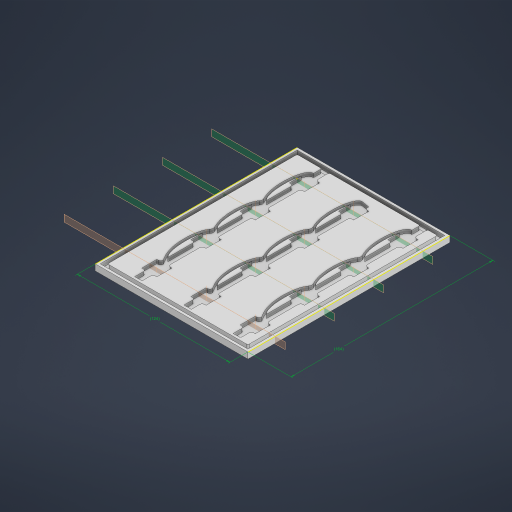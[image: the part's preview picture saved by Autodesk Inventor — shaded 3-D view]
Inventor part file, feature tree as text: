
AUTODESK INVENTOR PART (.ipt)
format: ipt  version: 2023 (Build 270158030, 158C)  size: 1,356,800 bytes
history: native  units: mm
features: other x13, sketch x8, plane x7, extrude x6, delete_face x5, fillet x3, direct_edit x3, pattern_linear x2, projected_geometry x2, move_body x2, chamfer x1
ambient origin geometry x8: Origin, YZ Plane, XZ Plane, XY Plane, X Axis, Y Axis, Z Axis, Center Point
bodies: Volumenkörper1 (feature_tree)
feature tree (52):
  extrude  "Extrusion1"  Depth=12.3mm
  extrude  "Extrusion2"  Depth=120.0mm
  extrude  "Extrusion3"  Depth=3.0mm TaperAngle=0.0deg
  chamfer  "Fase1"  Distance=2.0mm
  fillet  "Rundung1"  Radius=6.0mm
  pattern_linear  "Rechteckige Anordnung2"  Count1=3  [1 undecoded]
  extrude  "Extrusion5"  Depth=1.25mm
  direct_edit  "Direktbearbeitung1"
  sketch  "Sketch12"  dims[d18=10.0mm d19=0.0mm]
  extrude  "Extrusion11"  Depth=1.25mm
  delete_face  "Delete Face1"
  pattern_linear  "Rectangular Pattern4"  Spacing1=3.5mm  [1 undecoded]
  delete_face  "Delete Face2"
  fillet  "Fillet3"  Radius=8.5mm
  delete_face  "Delete Face3"
  delete_face  "Delete Face4"
  extrude  "Extrusion16"  Depth=1.25mm TaperAngle=0.0deg
  direct_edit  "Direct Edit3"
  delete_face  "Delete Face5"
  direct_edit  "Direct Edit4"
  fillet  "Fillet7"  Radius=30.0mm
  plane  "Work Plane1"
  plane  "Work Plane2"
  plane  "Work Plane3"
  plane  "Work Plane4"
  plane  "Work Plane5"
  plane  "Work Plane6"
  other  "Work Axis1"
  other  "Work Axis2"
  other  "Work Axis3"
  other  "Work Axis4"
  other  "Work Axis5"
  other  "Work Axis6"
  other  "Work Axis7"
  other  "Work Axis8"
  plane  "Work Plane7"
  other  "Work Axis9"
  other  "Work Axis10"
  other  "Work Axis11"
  sketch  "Sketch19"  dims[d33=40.0mm d35=40.0mm d49=3.0mm d50=2.0mm d51=3.5mm d52=0.0mm d53=8.5mm d54=0.0mm d55=0.0mm d124=3.5mm d125=0.0mm d126=30.0mm d128=40.0mm d129=30.0mm d131=40.0mm d139=3.0mm d162=2.0mm d163=10.0mm d164=0.0mm d165=-1.0mm d175=-2.5mm d176=0.0mm d177=0.0mm d181=1.25mm d182=124.0mm d183=164.0mm]
  sketch  "Skizze1"  dims[d0=12.3mm d1=12.3mm]
  sketch  "Skizze2"  dims[d2=30.0mm d4=40.0mm d5=40.0mm d7=40.0mm d10=120.0mm]
  sketch  "Skizze3"  dims[d11=160.0mm d12=3.0mm d13=0.0mm d14=2.0mm d15=0.0mm d16=6.0mm]
  sketch  "Skizze5"  dims[d17=27.0mm]
  other  "Image2"
  sketch  "Sketch13"  dims[d20=1.5mm d21=2.0mm d22=45.0deg]
  projected_geometry  "Projected Loop1"
  sketch  "Sketch18"  dims[d29=2.0mm d30=30.0mm d32=40.0mm]
  projected_geometry  "Projected Loop2"
  move_body  "Verschieben1"
  other  "Size1"
  move_body  "Move3"
note: 2 required parameter values undecoded (feature->parameter linkage not recoverable at this tier; creation-order binding heuristic only, values carry confidence <= 0.55)
